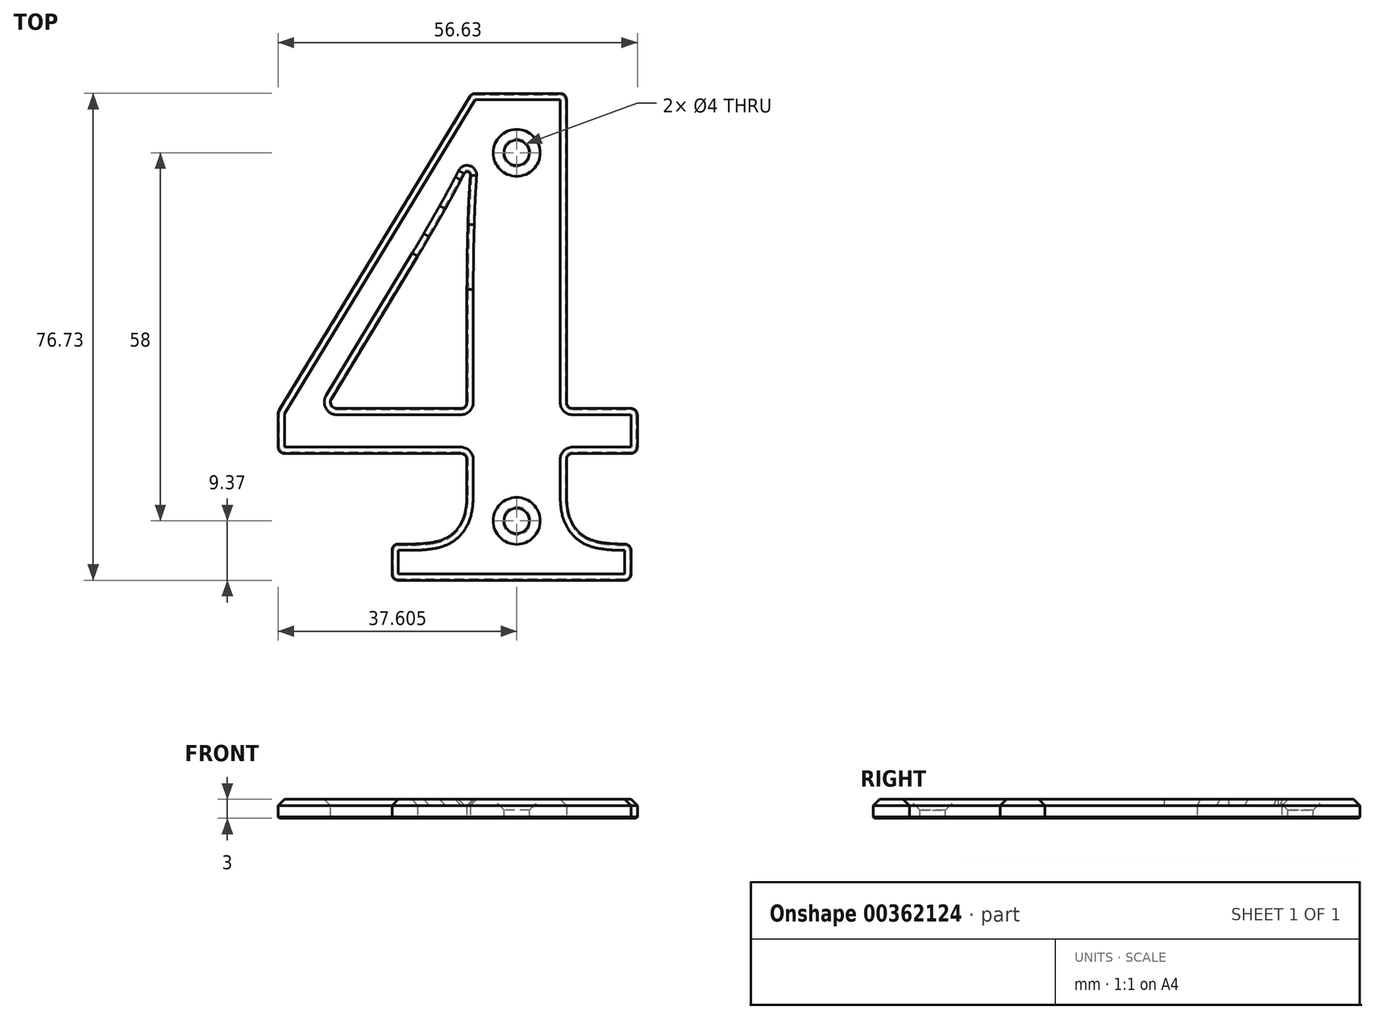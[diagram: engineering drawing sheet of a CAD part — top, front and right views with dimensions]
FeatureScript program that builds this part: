
annotation { "Feature Type Name" : "Feature", "Feature Type Description" : "" }
export const myFeature = defineFeature(function(context is Context, id is Id, definition is map)
    precondition{}
    {
        {
            var Q0;
            Q0=qCreatedBy(makeId("Top.planeOp"),FACE);
            var sketch = newSketch(context, id + "F0", { "sketchPlane" : qUnion([Q0])});
            skText(sketch, "E0", { "text": "4", "fontName": "NotoSerif-Bold.ttf"});
            const initialGuessF0  = {"E0": [-0.0325, 0, 1, 0, 0.07738]};
            skSetInitialGuess(sketch, initialGuessF0);
            skSolve(sketch);
        }
        {
            var Q0;
            Q0=makeQuery(id+"F0.imprint","IMPRINT",FACE,{"disambiguationData":[TD([[makeQuery(id+"F0.imprint","IMPRINT",EDGE,{"derivedFrom":sQuery(id+"F0.wireOp",EDGE,"E0.sketch_text.stroke-0")}),-1.0]])]});
            extrude(context, id + "F1", {"entities" : qUnion([Q0]), "depth" : 3 * mm, "offsetDistance" : 25 * mm});
        }
        {
            var Q0;
            Q0=makeQuery(id+"F1.opExtrude","SWEPT_EDGE",EDGE,{"disambiguationData":[OSD([sQuery(id+"F0.wireOp",EDGE,"E0.sketch_text.stroke-16"),sQuery(id+"F0.wireOp",EDGE,"E0.sketch_text.stroke-17")])]});
            var Q1;
            Q1=makeQuery(id+"F1.opExtrude","SWEPT_EDGE",EDGE,{"disambiguationData":[OSD([sQuery(id+"F0.wireOp",EDGE,"E0.sketch_text.stroke-15"),sQuery(id+"F0.wireOp",EDGE,"E0.sketch_text.stroke-16")])]});
            var Q2;
            Q2=makeQuery(id+"F1.opExtrude","SWEPT_EDGE",EDGE,{"disambiguationData":[OSD([sQuery(id+"F0.wireOp",EDGE,"E0.sketch_text.stroke-14"),sQuery(id+"F0.wireOp",EDGE,"E0.sketch_text.stroke-15")])]});
            var Q3;
            Q3=makeQuery(id+"F1.opExtrude","SWEPT_EDGE",EDGE,{"disambiguationData":[OSD([sQuery(id+"F0.wireOp",EDGE,"E0.sketch_text.stroke-8"),sQuery(id+"F0.wireOp",EDGE,"E0.sketch_text.stroke-9")])]});
            var Q4;
            Q4=makeQuery(id+"F1.opExtrude","SWEPT_EDGE",EDGE,{"disambiguationData":[OSD([sQuery(id+"F0.wireOp",EDGE,"E0.sketch_text.stroke-7"),sQuery(id+"F0.wireOp",EDGE,"E0.sketch_text.stroke-8")])]});
            var Q5;
            Q5=makeQuery(id+"F1.opExtrude","SWEPT_EDGE",EDGE,{"disambiguationData":[OSD([sQuery(id+"F0.wireOp",EDGE,"E0.sketch_text.stroke-6"),sQuery(id+"F0.wireOp",EDGE,"E0.sketch_text.stroke-7")])]});
            var Q6;
            Q6=makeQuery(id+"F1.opExtrude","SWEPT_EDGE",EDGE,{"disambiguationData":[OSD([sQuery(id+"F0.wireOp",EDGE,"E0.sketch_text.stroke-5"),sQuery(id+"F0.wireOp",EDGE,"E0.sketch_text.stroke-6")])]});
            var Q7;
            Q7=makeQuery(id+"F1.opExtrude","SWEPT_EDGE",EDGE,{"disambiguationData":[OSD([sQuery(id+"F0.wireOp",EDGE,"E0.sketch_text.stroke-0"),sQuery(id+"F0.wireOp",EDGE,"E0.sketch_text.stroke-22")])]});
            var Q8;
            Q8=makeQuery(id+"F1.opExtrude","SWEPT_EDGE",EDGE,{"disambiguationData":[OSD([sQuery(id+"F0.wireOp",EDGE,"E0.sketch_text.stroke-21"),sQuery(id+"F0.wireOp",EDGE,"E0.sketch_text.stroke-22")])]});
            var Q9;
            Q9=makeQuery(id+"F1.opExtrude","SWEPT_EDGE",EDGE,{"disambiguationData":[OSD([sQuery(id+"F0.wireOp",EDGE,"E0.sketch_text.stroke-20"),sQuery(id+"F0.wireOp",EDGE,"E0.sketch_text.stroke-21")])]});
            var Q10;
            Q10=makeQuery(id+"F1.opExtrude","SWEPT_EDGE",EDGE,{"disambiguationData":[OSD([sQuery(id+"F0.wireOp",EDGE,"E0.sketch_text.stroke-19"),sQuery(id+"F0.wireOp",EDGE,"E0.sketch_text.stroke-20")])]});
            var Q11;
            Q11=makeQuery(id+"F1.opExtrude","SWEPT_EDGE",EDGE,{"disambiguationData":[OSD([sQuery(id+"F0.wireOp",EDGE,"E0.sketch_text.stroke-18"),sQuery(id+"F0.wireOp",EDGE,"E0.sketch_text.stroke-19")])]});
            var Q12;
            Q12=makeQuery(id+"F1.opExtrude","SWEPT_EDGE",EDGE,{"disambiguationData":[OSD([sQuery(id+"F0.wireOp",EDGE,"E0.sketch_text.stroke-17"),sQuery(id+"F0.wireOp",EDGE,"E0.sketch_text.stroke-18")])]});
            var Q13;
            Q13=makeQuery(id+"F1.opExtrude","SWEPT_EDGE",EDGE,{"disambiguationData":[OSD([sQuery(id+"F0.wireOp",EDGE,"E0.sketch_text.stroke-29"),sQuery(id+"F0.wireOp",EDGE,"E0.sketch_text.stroke-30")])]});
            var Q14;
            Q14=makeQuery(id+"F1.opExtrude","SWEPT_EDGE",EDGE,{"disambiguationData":[OSD([sQuery(id+"F0.wireOp",EDGE,"E0.sketch_text.stroke-30"),sQuery(id+"F0.wireOp",EDGE,"E0.sketch_text.stroke-31")])]});
            fillet(context, id + "F2", {"entities" : qUnion([Q0, Q1, Q2, Q3, Q4, Q5, Q6, Q7, Q8, Q9, Q10, Q11, Q12, Q13, Q14]), "radius" : 1 * mm, "tangentPropagation" : true, "allowEdgeOverflow" : false});
        }
        {
            var Q0;
            Q0=makeQuery(id+"F1.opExtrude","CAP_FACE",FACE,{"disambiguationData":[OSD([sQuery(id+"F0.wireOp",EDGE,"E0.sketch_text.stroke-0"),sQuery(id+"F0.wireOp",EDGE,"E0.sketch_text.stroke-1"),sQuery(id+"F0.wireOp",EDGE,"E0.sketch_text.stroke-2"),sQuery(id+"F0.wireOp",EDGE,"E0.sketch_text.stroke-3"),sQuery(id+"F0.wireOp",EDGE,"E0.sketch_text.stroke-4"),sQuery(id+"F0.wireOp",EDGE,"E0.sketch_text.stroke-5"),sQuery(id+"F0.wireOp",EDGE,"E0.sketch_text.stroke-6"),sQuery(id+"F0.wireOp",EDGE,"E0.sketch_text.stroke-7"),sQuery(id+"F0.wireOp",EDGE,"E0.sketch_text.stroke-8"),sQuery(id+"F0.wireOp",EDGE,"E0.sketch_text.stroke-9"),sQuery(id+"F0.wireOp",EDGE,"E0.sketch_text.stroke-10"),sQuery(id+"F0.wireOp",EDGE,"E0.sketch_text.stroke-11"),sQuery(id+"F0.wireOp",EDGE,"E0.sketch_text.stroke-12"),sQuery(id+"F0.wireOp",EDGE,"E0.sketch_text.stroke-13"),sQuery(id+"F0.wireOp",EDGE,"E0.sketch_text.stroke-14"),sQuery(id+"F0.wireOp",EDGE,"E0.sketch_text.stroke-15"),sQuery(id+"F0.wireOp",EDGE,"E0.sketch_text.stroke-16"),sQuery(id+"F0.wireOp",EDGE,"E0.sketch_text.stroke-17"),sQuery(id+"F0.wireOp",EDGE,"E0.sketch_text.stroke-18"),sQuery(id+"F0.wireOp",EDGE,"E0.sketch_text.stroke-19"),sQuery(id+"F0.wireOp",EDGE,"E0.sketch_text.stroke-20"),sQuery(id+"F0.wireOp",EDGE,"E0.sketch_text.stroke-21"),sQuery(id+"F0.wireOp",EDGE,"E0.sketch_text.stroke-22"),sQuery(id+"F0.wireOp",EDGE,"E0.sketch_text.stroke-23"),sQuery(id+"F0.wireOp",EDGE,"E0.sketch_text.stroke-24"),sQuery(id+"F0.wireOp",EDGE,"E0.sketch_text.stroke-25"),sQuery(id+"F0.wireOp",EDGE,"E0.sketch_text.stroke-26"),sQuery(id+"F0.wireOp",EDGE,"E0.sketch_text.stroke-27"),sQuery(id+"F0.wireOp",EDGE,"E0.sketch_text.stroke-28"),sQuery(id+"F0.wireOp",EDGE,"E0.sketch_text.stroke-29"),sQuery(id+"F0.wireOp",EDGE,"E0.sketch_text.stroke-30"),sQuery(id+"F0.wireOp",EDGE,"E0.sketch_text.stroke-31")])],"isStart":false});
            var sketch = newSketch(context, id + "F3", { "sketchPlane" : qUnion([Q0])});
            skLineSegment(sketch, "E1", {"start": v(6.52, 76.72) * mm, "end": v(6.52, 0) * mm, "construction": true});
            skCircle(sketch, "E2", {"center": v(6.52, 67.37) * mm, "radius": 3.64 * mm});
            skCircle(sketch, "E3", {"center": v(6.52, 9.37) * mm, "radius": 4.44 * mm});
            skSolve(sketch);
        }
        {
            var Q0;
            Q0=sQuery(id+"F3.wireOp",VERTEX,"E2.center");
            var Q1;
            Q1=sQuery(id+"F3.wireOp",VERTEX,"E3.center");
            var Q2;
            Q2=makeQuery(id+"F1.opExtrude","SWEPT_BODY",BODY,{"disambiguationData":[OSD([sQuery(id+"F0.wireOp",EDGE,"E0.sketch_text.stroke-0"),sQuery(id+"F0.wireOp",EDGE,"E0.sketch_text.stroke-1"),sQuery(id+"F0.wireOp",EDGE,"E0.sketch_text.stroke-2"),sQuery(id+"F0.wireOp",EDGE,"E0.sketch_text.stroke-3"),sQuery(id+"F0.wireOp",EDGE,"E0.sketch_text.stroke-4"),sQuery(id+"F0.wireOp",EDGE,"E0.sketch_text.stroke-5"),sQuery(id+"F0.wireOp",EDGE,"E0.sketch_text.stroke-6"),sQuery(id+"F0.wireOp",EDGE,"E0.sketch_text.stroke-7"),sQuery(id+"F0.wireOp",EDGE,"E0.sketch_text.stroke-8"),sQuery(id+"F0.wireOp",EDGE,"E0.sketch_text.stroke-9"),sQuery(id+"F0.wireOp",EDGE,"E0.sketch_text.stroke-10"),sQuery(id+"F0.wireOp",EDGE,"E0.sketch_text.stroke-11"),sQuery(id+"F0.wireOp",EDGE,"E0.sketch_text.stroke-12"),sQuery(id+"F0.wireOp",EDGE,"E0.sketch_text.stroke-13"),sQuery(id+"F0.wireOp",EDGE,"E0.sketch_text.stroke-14"),sQuery(id+"F0.wireOp",EDGE,"E0.sketch_text.stroke-15"),sQuery(id+"F0.wireOp",EDGE,"E0.sketch_text.stroke-16"),sQuery(id+"F0.wireOp",EDGE,"E0.sketch_text.stroke-17"),sQuery(id+"F0.wireOp",EDGE,"E0.sketch_text.stroke-18"),sQuery(id+"F0.wireOp",EDGE,"E0.sketch_text.stroke-19"),sQuery(id+"F0.wireOp",EDGE,"E0.sketch_text.stroke-20"),sQuery(id+"F0.wireOp",EDGE,"E0.sketch_text.stroke-21"),sQuery(id+"F0.wireOp",EDGE,"E0.sketch_text.stroke-22"),sQuery(id+"F0.wireOp",EDGE,"E0.sketch_text.stroke-23"),sQuery(id+"F0.wireOp",EDGE,"E0.sketch_text.stroke-24"),sQuery(id+"F0.wireOp",EDGE,"E0.sketch_text.stroke-25"),sQuery(id+"F0.wireOp",EDGE,"E0.sketch_text.stroke-26"),sQuery(id+"F0.wireOp",EDGE,"E0.sketch_text.stroke-27"),sQuery(id+"F0.wireOp",EDGE,"E0.sketch_text.stroke-28"),sQuery(id+"F0.wireOp",EDGE,"E0.sketch_text.stroke-29"),sQuery(id+"F0.wireOp",EDGE,"E0.sketch_text.stroke-30"),sQuery(id+"F0.wireOp",EDGE,"E0.sketch_text.stroke-31")])]});
            hole(context, id + "F4", {"style" : HoleStyle.C_SINK, "endStyle" : HoleEndStyle.BLIND, "holeDiameter" : 4 * mm, "cSinkDiameter" : 7.4 * mm, "cSinkAngle" : 90 * degree, "majorDiameter" : 5 * mm, "holeDepth" : 20 * mm, "isTappedThrough" : true, "tappedDepth" : 12 * mm, "tapClearance" : 3, "locations" : qUnion([Q0, Q1]), "scope" : qUnion([Q2])});
        }
        {
            var Q0;
            Q0=makeQuery(id+"F1.opExtrude","SWEPT_EDGE",EDGE,{"disambiguationData":[OSD([sQuery(id+"F0.wireOp",EDGE,"E0.sketch_text.stroke-24"),sQuery(id+"F0.wireOp",EDGE,"E0.sketch_text.stroke-25")])]});
            fillet(context, id + "F5", {"entities" : qUnion([Q0]), "radius" : 0.5 * mm, "tangentPropagation" : true, "allowEdgeOverflow" : false});
        }
        {
            var Q0;
            Q0=makeQuery(id+"F1.opExtrude","CAP_FACE",FACE,{"disambiguationData":[OSD([sQuery(id+"F0.wireOp",EDGE,"E0.sketch_text.stroke-0"),sQuery(id+"F0.wireOp",EDGE,"E0.sketch_text.stroke-1"),sQuery(id+"F0.wireOp",EDGE,"E0.sketch_text.stroke-2"),sQuery(id+"F0.wireOp",EDGE,"E0.sketch_text.stroke-3"),sQuery(id+"F0.wireOp",EDGE,"E0.sketch_text.stroke-4"),sQuery(id+"F0.wireOp",EDGE,"E0.sketch_text.stroke-5"),sQuery(id+"F0.wireOp",EDGE,"E0.sketch_text.stroke-6"),sQuery(id+"F0.wireOp",EDGE,"E0.sketch_text.stroke-7"),sQuery(id+"F0.wireOp",EDGE,"E0.sketch_text.stroke-8"),sQuery(id+"F0.wireOp",EDGE,"E0.sketch_text.stroke-9"),sQuery(id+"F0.wireOp",EDGE,"E0.sketch_text.stroke-10"),sQuery(id+"F0.wireOp",EDGE,"E0.sketch_text.stroke-11"),sQuery(id+"F0.wireOp",EDGE,"E0.sketch_text.stroke-12"),sQuery(id+"F0.wireOp",EDGE,"E0.sketch_text.stroke-13"),sQuery(id+"F0.wireOp",EDGE,"E0.sketch_text.stroke-14"),sQuery(id+"F0.wireOp",EDGE,"E0.sketch_text.stroke-15"),sQuery(id+"F0.wireOp",EDGE,"E0.sketch_text.stroke-16"),sQuery(id+"F0.wireOp",EDGE,"E0.sketch_text.stroke-17"),sQuery(id+"F0.wireOp",EDGE,"E0.sketch_text.stroke-18"),sQuery(id+"F0.wireOp",EDGE,"E0.sketch_text.stroke-19"),sQuery(id+"F0.wireOp",EDGE,"E0.sketch_text.stroke-20"),sQuery(id+"F0.wireOp",EDGE,"E0.sketch_text.stroke-21"),sQuery(id+"F0.wireOp",EDGE,"E0.sketch_text.stroke-22"),sQuery(id+"F0.wireOp",EDGE,"E0.sketch_text.stroke-23"),sQuery(id+"F0.wireOp",EDGE,"E0.sketch_text.stroke-24"),sQuery(id+"F0.wireOp",EDGE,"E0.sketch_text.stroke-25"),sQuery(id+"F0.wireOp",EDGE,"E0.sketch_text.stroke-26"),sQuery(id+"F0.wireOp",EDGE,"E0.sketch_text.stroke-27"),sQuery(id+"F0.wireOp",EDGE,"E0.sketch_text.stroke-28"),sQuery(id+"F0.wireOp",EDGE,"E0.sketch_text.stroke-29"),sQuery(id+"F0.wireOp",EDGE,"E0.sketch_text.stroke-30"),sQuery(id+"F0.wireOp",EDGE,"E0.sketch_text.stroke-31")])],"isStart":true});
            chamfer(context, id + "F6", {"entities" : qUnion([Q0]), "width" : 0.2 * mm, "tangentPropagation" : true});
        }
        {
            var Q0;
            Q0=makeQuery(id+"F1.opExtrude","CAP_EDGE",EDGE,{"disambiguationData":[OSD([sQuery(id+"F0.wireOp",EDGE,"E0.sketch_text.stroke-17")])],"isStart":false});
            var Q1;
            Q1=makeQuery(id+"F1.opExtrude","CAP_EDGE",EDGE,{"disambiguationData":[OSD([sQuery(id+"F0.wireOp",EDGE,"E0.sketch_text.stroke-29")])],"isStart":false});
            chamfer(context, id + "F7", {"entities" : qUnion([Q0, Q1]), "width" : 1 * mm, "tangentPropagation" : true});
        }
    });
